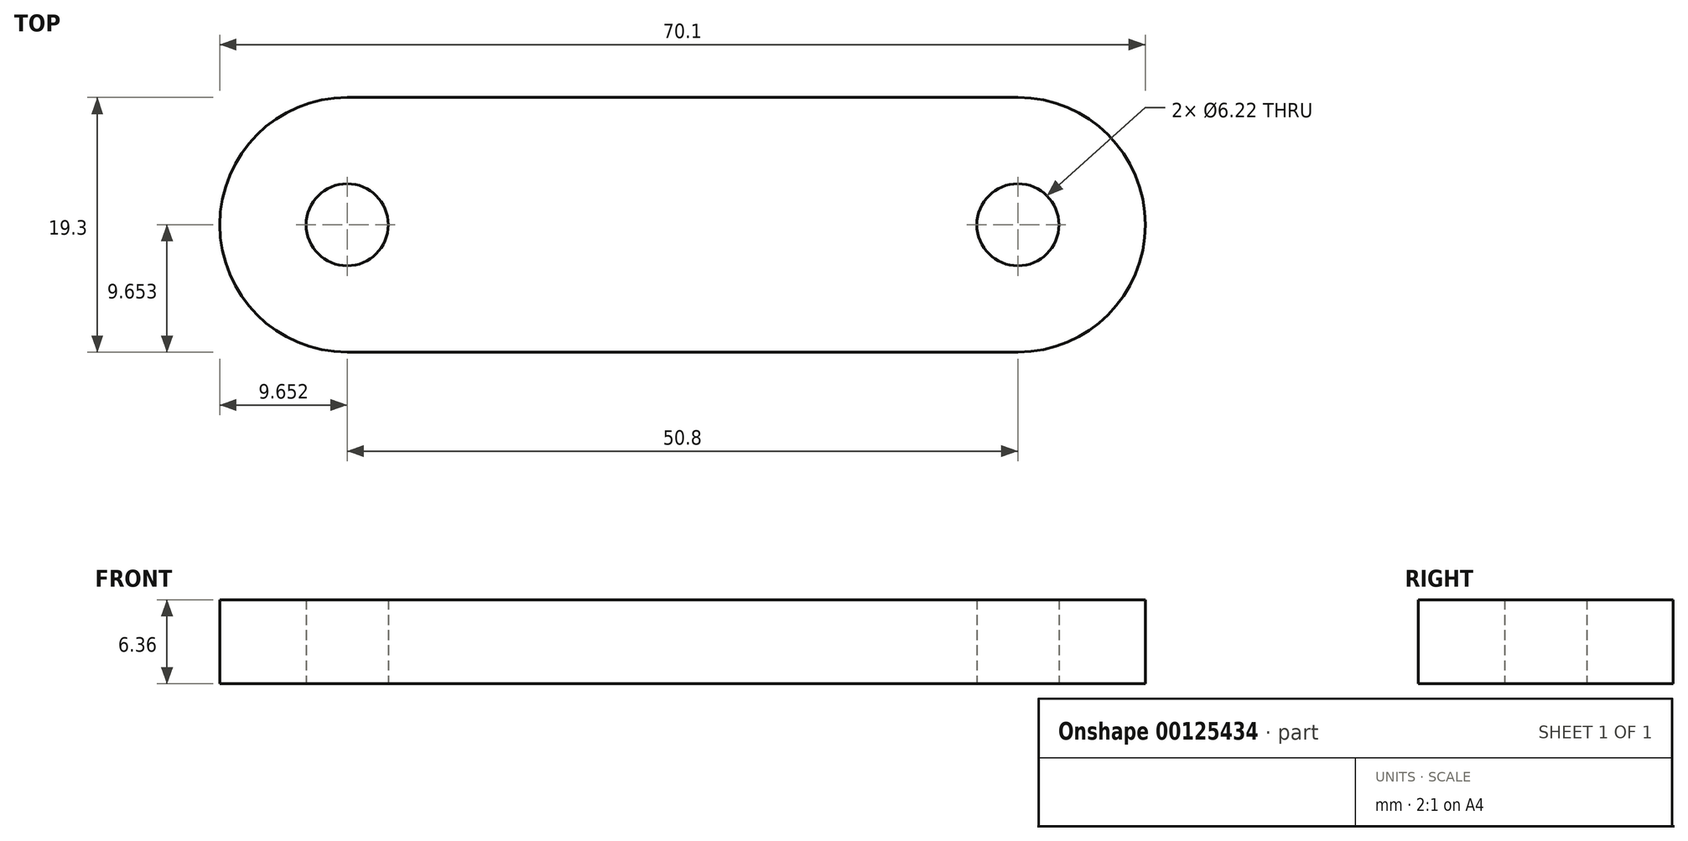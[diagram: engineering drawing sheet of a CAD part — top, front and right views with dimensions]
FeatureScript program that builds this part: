
annotation { "Feature Type Name" : "Feature", "Feature Type Description" : "" }
export const myFeature = defineFeature(function(context is Context, id is Id, definition is map)
    precondition{}
    {
        {
            var Q0;
            Q0=qCreatedBy(makeId("Top.planeOp"),FACE);
            var sketch = newSketch(context, id + "F0", { "sketchPlane" : qUnion([Q0])});
            skLineSegment(sketch, "E0", {"start": v(-51.9, 38.84) * mm, "end": v(-1.1, 38.84) * mm});
            skLineSegment(sketch, "E1", {"start": v(-51.9, 19.54) * mm, "end": v(-1.1, 19.54) * mm});
            skArc(sketch, "E2", {"start": v(-51.9, 38.84) * mm, "mid": v(-61.56, 29.2) * mm, "end": v(-51.9, 19.54) * mm});
            skArc(sketch, "E3", {"start": v(-1.1, 19.54) * mm, "mid": v(8.54, 29.2) * mm, "end": v(-1.1, 38.84) * mm});
            skCircle(sketch, "E4", {"center": v(-51.9, 29.2) * mm, "radius": 3.11 * mm});
            skCircle(sketch, "E5", {"center": v(-1.1, 29.2) * mm, "radius": 3.11 * mm});
            skSolve(sketch);
        }
        {
            var Q0;
            Q0=makeQuery(id+"F0.imprint","IMPRINT",FACE,{"disambiguationData":[TD([[makeQuery(id+"F0.imprint","IMPRINT",EDGE,{"derivedFrom":sQuery(id+"F0.wireOp",EDGE,"E0")}),-1.0]])]});
            extrude(context, id + "F1", {"entities" : qUnion([Q0]), "endBound" : BoundingType.SYMMETRIC, "depth" : 6.35 * mm});
        }
    });
